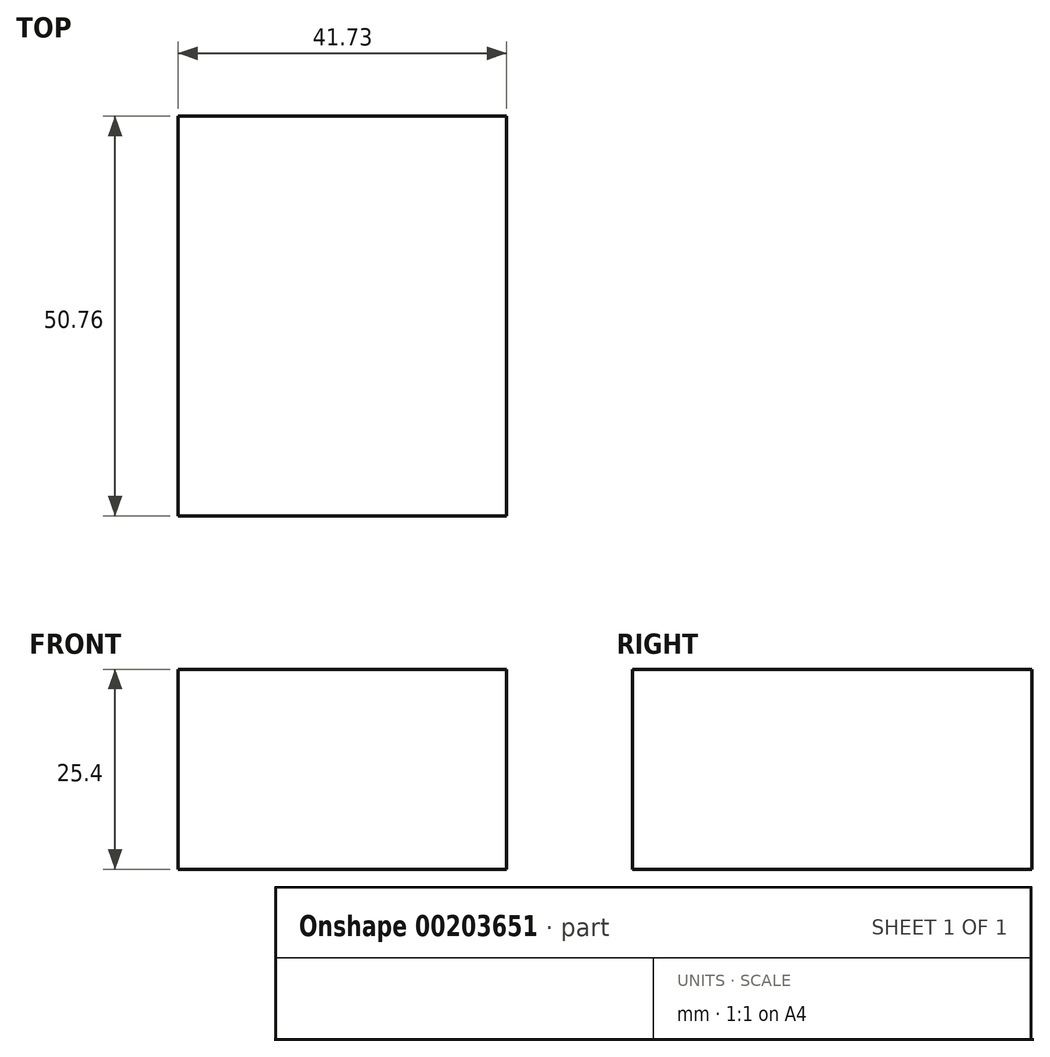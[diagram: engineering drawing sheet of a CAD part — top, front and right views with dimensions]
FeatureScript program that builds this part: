
annotation { "Feature Type Name" : "Feature", "Feature Type Description" : "" }
export const myFeature = defineFeature(function(context is Context, id is Id, definition is map)
    precondition{}
    {
        {
            var Q0;
            Q0=qCreatedBy(makeId("Top.planeOp"),FACE);
            var sketch = newSketch(context, id + "F0", { "sketchPlane" : qUnion([Q0])});
            skLineSegment(sketch, "E0.bottom", {"start": v(41.73, 50.76) * mm, "end": v(0, 50.76) * mm});
            skLineSegment(sketch, "E0.top", {"start": v(41.73, 0) * mm, "end": v(0, 0) * mm});
            skLineSegment(sketch, "E0.left", {"start": v(41.73, 50.76) * mm, "end": v(41.73, 0) * mm});
            skLineSegment(sketch, "E0.right", {"start": v(0, 50.76) * mm, "end": v(0, 0) * mm});
            skSolve(sketch);
        }
        {
            var Q0;
            Q0=makeQuery(id+"F0.imprint","IMPRINT",FACE,{"disambiguationData":[TD([[makeQuery(id+"F0.imprint","IMPRINT",EDGE,{"derivedFrom":sQuery(id+"F0.wireOp",EDGE,"E0.bottom")}),1.0]])]});
            extrude(context, id + "F1", {"entities" : qUnion([Q0]), "depth" : 25.4 * mm});
        }
    });
